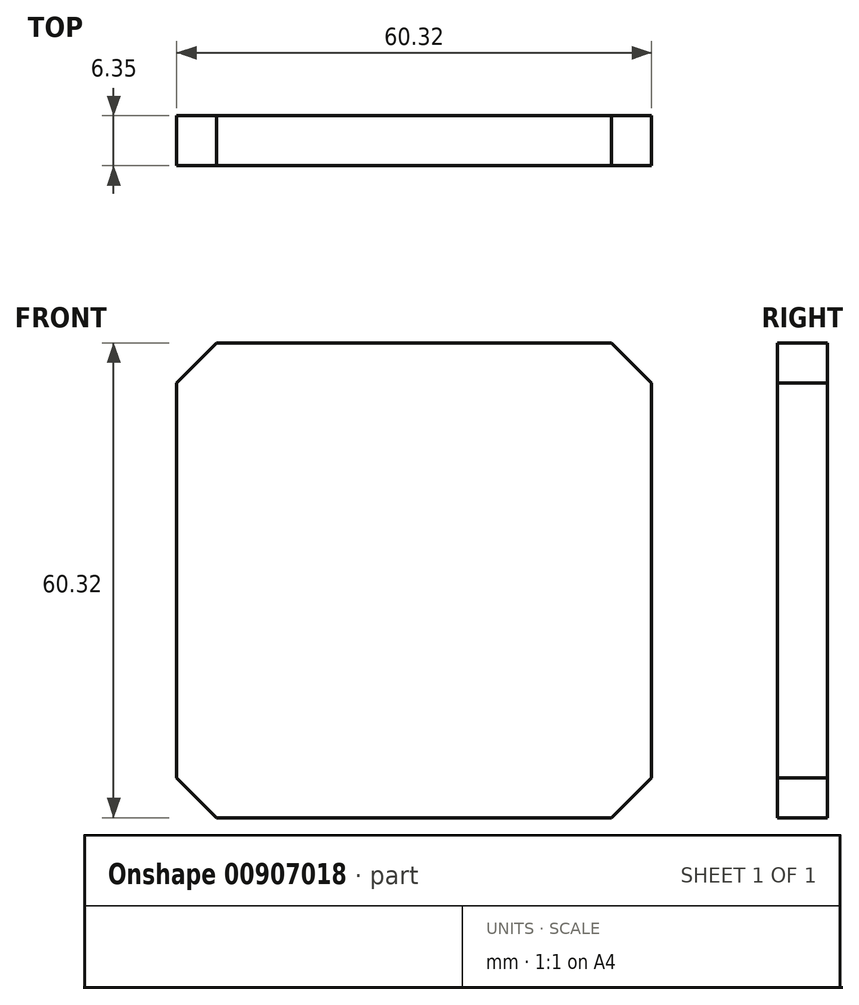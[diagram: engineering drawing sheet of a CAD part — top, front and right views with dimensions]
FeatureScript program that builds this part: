
annotation { "Feature Type Name" : "Feature", "Feature Type Description" : "" }
export const myFeature = defineFeature(function(context is Context, id is Id, definition is map)
    precondition{}
    {
        {
            var Q0;
            Q0=qCreatedBy(makeId("Front.planeOp"),FACE);
            var sketch = newSketch(context, id + "F0", { "sketchPlane" : qUnion([Q0])});
            skLineSegment(sketch, "E0.bottom", {"start": v(-30.16, 30.16) * mm, "end": v(30.16, 30.16) * mm});
            skLineSegment(sketch, "E0.top", {"start": v(-30.16, -30.16) * mm, "end": v(30.16, -30.16) * mm});
            skLineSegment(sketch, "E0.left", {"start": v(-30.16, 30.16) * mm, "end": v(-30.16, -30.16) * mm});
            skLineSegment(sketch, "E0.right", {"start": v(30.16, 30.16) * mm, "end": v(30.16, -30.16) * mm});
            skPoint(sketch, "E0.middle", {"position": v(0, 0) * mm});
            skSolve(sketch);
        }
        {
            var Q0;
            Q0=makeQuery(id+"F0.imprint","IMPRINT",FACE,{"disambiguationData":[TD([[makeQuery(id+"F0.imprint","IMPRINT",EDGE,{"derivedFrom":sQuery(id+"F0.wireOp",EDGE,"E0.bottom")}),-1.0]])]});
            extrude(context, id + "F1", {"entities" : qUnion([Q0]), "depth" : 6.35 * mm, "offsetDistance" : 25.4 * mm});
        }
        {
            var Q0;
            Q0=makeQuery(id+"F1.opExtrude","SWEPT_EDGE",EDGE,{"disambiguationData":[OSD([sQuery(id+"F0.wireOp",EDGE,"E0.bottom"),sQuery(id+"F0.wireOp",EDGE,"E0.left")])]});
            var Q1;
            Q1=makeQuery(id+"F1.opExtrude","SWEPT_EDGE",EDGE,{"disambiguationData":[OSD([sQuery(id+"F0.wireOp",EDGE,"E0.bottom"),sQuery(id+"F0.wireOp",EDGE,"E0.right")])]});
            var Q2;
            Q2=makeQuery(id+"F1.opExtrude","SWEPT_EDGE",EDGE,{"disambiguationData":[OSD([sQuery(id+"F0.wireOp",EDGE,"E0.top"),sQuery(id+"F0.wireOp",EDGE,"E0.right")])]});
            var Q3;
            Q3=makeQuery(id+"F1.opExtrude","SWEPT_EDGE",EDGE,{"disambiguationData":[OSD([sQuery(id+"F0.wireOp",EDGE,"E0.top"),sQuery(id+"F0.wireOp",EDGE,"E0.left")])]});
            chamfer(context, id + "F2", {"entities" : qUnion([Q0, Q1, Q2, Q3]), "width" : 5.08 * mm, "tangentPropagation" : true});
        }
    });
